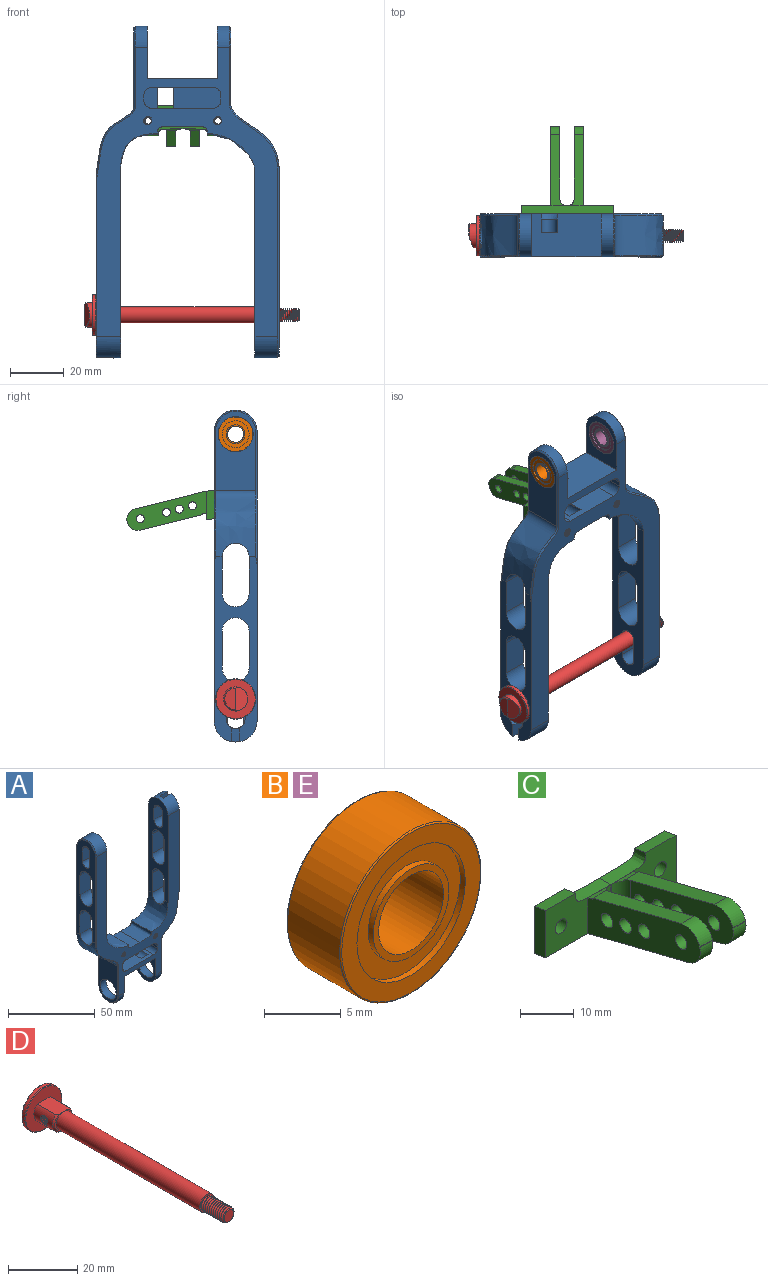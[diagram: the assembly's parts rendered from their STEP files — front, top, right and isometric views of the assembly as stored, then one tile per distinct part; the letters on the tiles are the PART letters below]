
ASSEMBLY  parts=5 mates=6
PART A: 93 faces, bbox 69.1x16.9x123.8 mm
  f0: plane 107.79x67.84mm, normal (0,1,0), area 2068.3mm2, adj f2,f7,f8,f10,f11,f12,f14,f17
  f1: cylinder r=3mm len=11.6mm, axis (0,1,0), area 58mm2, adj f2,f4,f5,f6,f60,f62,f63,f68
  f2: cone r=5mm half-angle=45deg, axis (0,1,0), area 8.4mm2, adj f0,f1,f67,f69
  f3: plane 22.7x8mm, normal (0,0,-1), area 148mm2, adj f5,f6,f9,f50,f55,f62,f63,f64
  f4: plane 22.7x8mm, normal (0,0,1), area 150.1mm2, adj f1,f5,f6,f9,f52,f53,f60
  f5: plane 17.84x7.8mm, normal (0,-1,0), area 133.9mm2, adj f1,f3,f4,f50,f51,f52,f62
  f6: plane 7.8x5.24mm, normal (0,-1,0), area 35.6mm2, adj f1,f3,f4,f53,f54,f55,f63
  f7: cylinder r=1.2mm len=16mm, axis (0,-1,0), area 20.2mm2, adj f0,f9,f58,f59
  f8: cylinder r=1.2mm len=16mm, axis (0,-1,0), area 20.2mm2, adj f0,f9,f56,f57
  f9: plane 107.79x67.84mm, normal (0,-1,0), area 2002.5mm2, adj f3,f4,f7,f8,f10,f11,f12,f14
  f10: plane 68.86x16mm, normal (1,0,0), area 572.6mm2, adj f0,f9,f11,f21,f35,f36,f37,f38
  f11: cylinder r=8mm len=16mm, axis (1,0,0), area 206.6mm2, adj f0,f9,f10,f14,f47,f48,f49
  f12: plane 69x16mm, normal (1,0,0), area 600.9mm2, adj f0,f9,f25,f26,f31,f32,f33,f34
  f13: plane 68.5x15mm, normal (-1,0,0), area 527.7mm2, adj f15,f31,f32,f33,f34,f43,f44,f45
  f14: plane 69x16mm, normal (-1,0,0), area 589.2mm2, adj f0,f9,f11,f22,f35,f36,f37,f38
  f15: extruded ~25.4x18mm, area 454.7mm2, adj f13,f16,f31,f75,f76
  f16: plane 28.5x15mm, normal (-1,0,0), area 270.6mm2, adj f15,f30,f72,f73,f74
  f17: plane 19.6x16mm, normal (1,0,0), area 153.4mm2, adj f0,f9,f18,f28,f30
  f18: plane 26x16mm, normal (0,0,-1), area 375.4mm2, adj f0,f9,f17,f19,f69,f70,f71
  f19: plane 19.6x16mm, normal (-1,0,0), area 153.4mm2, adj f0,f9,f18,f27,f29
  f20: plane 29.5x15mm, normal (1,0,0), area 285.6mm2, adj f21,f29,f81,f82,f83
  f21: extruded ~24.45x15mm, area 410.1mm2, adj f10,f20,f38,f80,f84
  f22: extruded ~16x14.45mm, area 334.6mm2, adj f0,f9,f14,f23,f38
  f23: extruded ~16x9.2mm, area 176.4mm2, adj f0,f9,f22,f24
  f24: extruded ~16x9.2mm, area 176.4mm2, adj f0,f9,f23,f25
  f25: extruded ~17.8x16mm, area 360.2mm2, adj f0,f9,f12,f24,f31
  f26: cylinder r=8mm len=16mm, axis (1,0,0), area 213.6mm2, adj f0,f9,f12,f79
  f27: cylinder r=8mm len=16mm, axis (-1,0,0), area 113.1mm2, adj f0,f9,f19,f82
  f28: cylinder r=8mm len=16mm, axis (-1,0,0), area 113.1mm2, adj f0,f9,f17,f72
  f29: cylinder r=6.5mm len=13mm, axis (1,0,0), area 204.2mm2, adj f19,f20
  f30: cylinder r=6.5mm len=13mm, axis (1,0,0), area 204.2mm2, adj f16,f17
  f31: cylinder r=5mm len=10.33mm, axis (1,0,0), area 148.4mm2, adj f12,f13,f15,f25,f32,f34
  f32: plane 13.7x9mm, normal (0,1,0), area 123.3mm2, adj f12,f13,f31,f33
  f33: cylinder r=5mm len=10mm, axis (1,0,0), area 141.4mm2, adj f12,f13,f32,f34
  f34: plane 13.7x9mm, normal (0,-1,0), area 123.3mm2, adj f12,f13,f31,f33
  f35: plane 13.7x9mm, normal (0,-1,0), area 123.3mm2, adj f10,f14,f36,f38
  f36: cylinder r=5mm len=10mm, axis (1,0,0), area 141.4mm2, adj f10,f14,f35,f37
  f37: plane 13.7x9mm, normal (0,1,0), area 123.3mm2, adj f10,f14,f36,f38
  f38: cylinder r=5mm len=10mm, axis (1,0,0), area 137mm2, adj f10,f14,f21,f22,f35,f37
  f39: cylinder r=5mm len=10mm, axis (1,0,0), area 141.4mm2, adj f10,f14,f40,f42
  f40: plane 13.7x9mm, normal (0,-1,0), area 123.3mm2, adj f10,f14,f39,f41
  f41: cylinder r=5mm len=10mm, axis (1,0,0), area 141.4mm2, adj f10,f14,f40,f42
  f42: plane 13.7x9mm, normal (0,1,0), area 123.3mm2, adj f10,f14,f39,f41
  f43: plane 13.7x9mm, normal (0,1,0), area 123.3mm2, adj f12,f13,f44,f46
  f44: cylinder r=5mm len=10mm, axis (1,0,0), area 141.4mm2, adj f12,f13,f43,f45
  f45: plane 13.7x9mm, normal (0,-1,0), area 123.3mm2, adj f12,f13,f44,f46
  f46: cylinder r=5mm len=10mm, axis (1,0,0), area 141.4mm2, adj f12,f13,f43,f45
  f47: plane 6.5x5.2mm, normal (0,-1,0), area 33.8mm2, adj f10,f11,f49,f88
  f48: plane 6.5x5.2mm, normal (0,1,0), area 33.8mm2, adj f10,f11,f49,f88
  f49: plane 5.34x3mm, normal (1,0,0), area 15.2mm2, adj f11,f47,f48,f88
  f50: cylinder r=3mm len=8mm, axis (0,-1,0), area 37.7mm2, adj f3,f5,f9,f51
  f51: plane 8x1.8mm, normal (1,0,0), area 14.4mm2, adj f5,f9,f50,f52
  f52: cylinder r=3mm len=8mm, axis (0,-1,0), area 37.7mm2, adj f4,f5,f9,f51
  f53: cylinder r=3mm len=8mm, axis (0,-1,0), area 37.7mm2, adj f4,f6,f9,f54
  f54: plane 8x1.8mm, normal (-1,0,0), area 14.4mm2, adj f6,f9,f53,f55
  f55: cylinder r=3mm len=8mm, axis (0,-1,0), area 37.7mm2, adj f3,f6,f9,f54
  f56: bspline ~16.5x3.75mm, area 138.9mm2, adj f0,f8,f9,f57
  f57: bspline ~16.58x3.75mm, area 139mm2, adj f0,f8,f9,f56
  f58: bspline ~16.5x3.75mm, area 138.9mm2, adj f0,f7,f9,f59
  f59: bspline ~16.58x3.75mm, area 139mm2, adj f0,f7,f9,f58
  f60: plane 5.62x1.95mm, normal (0,1,0), area 8mm2, adj f1,f4
  f61: cylinder r=3mm len=11.6mm, axis (0,1,0), area 109.3mm2, adj f62,f63,f64,f65
  f62: plane 11.6x7mm, normal (1,0,0), area 43.4mm2, adj f1,f3,f5,f61,f64,f66
  f63: plane 11.6x7mm, normal (-1,0,0), area 43.4mm2, adj f1,f3,f6,f61,f64,f67
  f64: plane 6x3.25mm, normal (0,1,0), area 15.6mm2, adj f3,f61,f62,f63
  f65: cone r=5mm half-angle=45deg, axis (0,1,0), area 35.5mm2, adj f0,f61,f66,f67
  f66: plane 7x2mm, normal (0.71,0.71,0), area 19.8mm2, adj f0,f62,f65,f68
  f67: plane 7x2mm, normal (-0.71,0.71,0), area 19.8mm2, adj f0,f2,f63,f65
  f68: cone r=5mm half-angle=45deg, axis (0,1,0), area 8.4mm2, adj f0,f1,f66,f71
  f69: plane 7x3.53mm, normal (-1,0,0), area 20.9mm2, adj f0,f1,f2,f18,f70
  f70: plane 5.8x3.53mm, normal (0,1,0), area 10.9mm2, adj f1,f18,f69,f71
  f71: plane 7x3.53mm, normal (1,0,0), area 20.9mm2, adj f0,f1,f18,f68,f70
  f72: cone r=7.5mm half-angle=45deg, axis (1,0,0), area 17.2mm2, adj f16,f28,f73,f74
  f73: plane 21x0.5mm, normal (-0.71,-0.71,0), area 14.8mm2, adj f9,f16,f72,f75
  f74: plane 21x0.5mm, normal (-0.71,0.71,0), area 14.8mm2, adj f0,f16,f72,f76
  f75: bspline ~25.4x18.51mm, area 23.2mm2, adj f9,f15,f73,f77
  f76: bspline ~25.4x18.51mm, area 23.2mm2, adj f0,f15,f74,f78
  f77: plane 61x0.5mm, normal (-0.71,-0.71,0), area 43.1mm2, adj f9,f13,f75,f79
  f78: plane 61x0.5mm, normal (-0.71,0.71,0), area 43.1mm2, adj f0,f13,f76,f79
  f79: cone r=7.5mm half-angle=45deg, axis (1,0,0), area 17.2mm2, adj f13,f26,f77,f78
  f80: bspline ~28.98x15.28mm, area 22.2mm2, adj f9,f10,f21,f81
  f81: plane 22x0.5mm, normal (0.71,-0.71,0), area 15.6mm2, adj f9,f20,f80,f82
  f82: cone r=7.5mm half-angle=45deg, axis (-1,0,0), area 17.2mm2, adj f20,f27,f81,f83
  f83: plane 22x0.5mm, normal (0.71,0.71,0), area 15.6mm2, adj f0,f20,f82,f84
  f84: bspline ~28.98x15.28mm, area 22.2mm2, adj f0,f10,f21,f83
  f85: plane 9x8mm, normal (0,-1,0), area 72mm2, adj f10,f14,f87,f88
  f86: plane 9x8mm, normal (0,1,0), area 72mm2, adj f10,f14,f87,f88
  f87: cylinder r=3.5mm len=9mm, axis (1,0,0), area 99mm2, adj f10,f14,f85,f86
  f88: cylinder r=3.5mm len=9mm, axis (1,0,0), area 78.8mm2, adj f10,f14,f47,f48,f49,f85,f86
  f89: cylinder r=3mm len=9mm, axis (-1,0,0), area 84.8mm2, adj f12,f13,f90,f92
  f90: plane 9x9mm, normal (0,-1,0), area 81mm2, adj f12,f13,f89,f91
  f91: cylinder r=3mm len=9mm, axis (-1,0,0), area 84.8mm2, adj f12,f13,f90,f92
  f92: plane 9x9mm, normal (0,1,0), area 81mm2, adj f12,f13,f89,f91
PART B: 14 faces, bbox 14.1x5x14.1 mm
  f0: plane 7x7mm, normal (0,1,0), area 10.2mm2, adj f2,f9
  f1: plane 7x7mm, normal (0,-1,0), area 10.2mm2, adj f2,f6
  f2: cylinder r=3mm len=6mm, axis (0,1,0), area 94.2mm2, adj f0,f1
  f3: cylinder r=6.5mm len=13mm, axis (0,1,0), area 196mm2, adj f12,f13
  f4: plane 12.8x12.8mm, normal (0,-1,0), area 50.1mm2, adj f8,f12
  f5: plane 12.8x12.8mm, normal (0,1,0), area 50.1mm2, adj f10,f13
  f6: cylinder r=3.5mm len=7mm, axis (0,1,0), area 10.1mm2, adj f1,f7
  f7: plane 10x10mm, normal (0,-1,0), area 40.1mm2, adj f6,f8
  f8: cylinder r=5mm len=10mm, axis (0,1,0), area 14.4mm2, adj f4,f7
  f9: cylinder r=3.5mm len=7mm, axis (0,-1,0), area 11mm2, adj f0,f11
  f10: cylinder r=5mm len=10mm, axis (0,-1,0), area 15.7mm2, adj f5,f11
  f11: plane 10x10mm, normal (0,1,0), area 40.1mm2, adj f9,f10
  f12: torus R=6.4mm, axis (0,-1,0), area 6.4mm2, adj f3,f4
  f13: torus R=6.4mm, axis (0,-1,0), area 6.4mm2, adj f3,f5
PART C: 43 faces, bbox 34.2x32.4x15.1 mm
  f0: plane 8.07x0.3mm, normal (0,-1,0), area 2.4mm2, adj f11,f12,f19,f39,f40
  f1: plane 17.08x10.7mm, normal (0,-1,0), area 104mm2, adj f2,f12,f13,f14,f19,f21,f28
  f2: plane 5.85x1.21mm, normal (0,0.24,0.97), area 5.4mm2, adj f1,f3,f28,f39
  f3: plane 3.72x0.07mm, normal (0,0.97,-0.24), area 0.3mm2, adj f2,f28,f39,f41
  f4: plane 23.1x5.77mm, normal (0,0.24,0.97), area 79.8mm2, adj f28,f33,f35,f39,f41
  f5: plane 3.35x0.1mm, normal (0,-0.97,0.24), area 0.3mm2, adj f28,f33,f35,f36
  f6: plane 26.39x6.58mm, normal (0,-0.24,-0.97), area 92.5mm2, adj f19,f28,f33,f36,f39
  f7: cylinder r=1.5mm len=3.35mm, axis (1,0,0), area 31.6mm2, adj f28,f33
  f8: cylinder r=1.5mm len=3.35mm, axis (1,0,0), area 31.6mm2, adj f28,f33
  f9: cylinder r=1.5mm len=3.35mm, axis (1,0,0), area 31.6mm2, adj f28,f33
  f10: cylinder r=1.5mm len=3.35mm, axis (1,0,0), area 31.6mm2, adj f28,f33
  f11: extruded ~9.2x3mm, area 32mm2, adj f0,f12,f17,f18,f20
  f12: extruded ~9.2x3mm, area 32mm2, adj f0,f1,f11,f18,f21
  f13: plane 11.2x3mm, normal (-1,0,0), area 32.1mm2, adj f1,f18,f19,f21
  f14: cylinder r=1.55mm len=3.1mm, axis (0,1,0), area 29.2mm2, adj f1,f18
  f15: plane 11.2x3mm, normal (1,0,0), area 32.1mm2, adj f17,f18,f19,f20
  f16: cylinder r=1.55mm len=3.1mm, axis (0,1,0), area 29.2mm2, adj f17,f18
  f17: plane 17.12x10.7mm, normal (0,-1,0), area 104mm2, adj f11,f15,f16,f19,f20,f22,f27
  f18: plane 34.2x11.2mm, normal (0,1,0), area 314mm2, adj f11,f12,f13,f14,f15,f16,f19,f20
  f19: plane 34.2x3mm, normal (0,-0.16,-0.99), area 104mm2, adj f0,f1,f6,f13,f15,f17,f18,f26
  f20: plane 7.94x3.02mm, normal (0,0.16,0.99), area 24.1mm2, adj f11,f15,f17,f18
  f21: plane 7.9x3.02mm, normal (0,0.16,0.99), area 24mm2, adj f1,f12,f13,f18
  f22: plane 5.85x1.21mm, normal (0,0.24,0.97), area 5.4mm2, adj f17,f23,f27,f40
  f23: plane 3.72x0.07mm, normal (0,0.97,-0.24), area 0.3mm2, adj f22,f27,f40,f42
  f24: plane 23.1x5.77mm, normal (0,0.24,0.97), area 79.8mm2, adj f27,f34,f37,f40,f42
  f25: plane 3.35x0.1mm, normal (0,-0.97,0.24), area 0.3mm2, adj f27,f34,f37,f38
  f26: plane 26.39x6.58mm, normal (0,-0.24,-0.97), area 92.5mm2, adj f19,f27,f34,f38,f40
  f27: plane 29.42x14.56mm, normal (1,0,0), area 209mm2, adj f17,f22,f23,f24,f25,f26,f29,f30
  f28: plane 29.42x14.56mm, normal (-1,0,0), area 209mm2, adj f1,f2,f3,f4,f5,f6,f7,f8
  f29: cylinder r=1.5mm len=3.35mm, axis (1,0,0), area 31.6mm2, adj f27,f34
  f30: cylinder r=1.5mm len=3.35mm, axis (1,0,0), area 31.6mm2, adj f27,f34
  f31: cylinder r=1.5mm len=3.35mm, axis (1,0,0), area 31.6mm2, adj f27,f34
  f32: cylinder r=1.5mm len=3.35mm, axis (1,0,0), area 31.6mm2, adj f27,f34
  f33: plane 26.92x13.94mm, normal (1,0,0), area 188.5mm2, adj f4,f5,f6,f7,f8,f9,f10,f35
  f34: plane 26.92x13.94mm, normal (-1,0,0), area 188.5mm2, adj f24,f25,f26,f29,f30,f31,f32,f37
  f35: cylinder r=4mm len=4.85mm, axis (-1,0,0), area 21mm2, adj f4,f5,f28,f33
  f36: cylinder r=4mm len=4.85mm, axis (-1,0,0), area 21mm2, adj f5,f6,f28,f33
  f37: cylinder r=4mm len=4.85mm, axis (-1,0,0), area 21mm2, adj f24,f25,f27,f34
  f38: cylinder r=4mm len=4.85mm, axis (-1,0,0), area 21mm2, adj f25,f26,f27,f34
  f39: cylinder r=2.5mm len=8.97mm, axis (0,0,1), area 32.1mm2, adj f0,f2,f3,f4,f6,f33,f41
  f40: cylinder r=2.5mm len=8.97mm, axis (0,0,-1), area 32.1mm2, adj f0,f22,f23,f24,f26,f34,f42
  f41: plane 3.72x0.24mm, normal (0,0.86,0.52), area 1mm2, adj f3,f4,f28,f39
  f42: plane 3.72x0.24mm, normal (0,0.86,0.52), area 1mm2, adj f23,f24,f27,f40
PART D: 26 faces, bbox 15.1x80.4x15.1 mm
  f0: plane 8x4mm, normal (0,1,0), area 25.1mm2, adj f1,f25
  f1: cone r=4mm half-angle=45deg, axis (0,-1,0), area 10.3mm2, adj f0,f2,f25
  f2: cylinder r=4.5mm len=9mm, axis (0,-1,0), area 55.3mm2, adj f1,f3,f25
  f3: plane 14.6x14.6mm, normal (0,1,0), area 103.8mm2, adj f2,f4
  f4: cone r=7.5mm half-angle=45deg, axis (0,-1,0), area 13.2mm2, adj f3,f5
  f5: cylinder r=7.5mm len=15mm, axis (0,1,0), area 54.2mm2, adj f4,f6
  f6: cone r=7.3mm half-angle=45deg, axis (0,1,0), area 13.2mm2, adj f5,f7
  f7: plane 14.6x14.6mm, normal (0,-1,0), area 120.8mm2, adj f6,f8,f19
  f8: plane 8.06x5.36mm, normal (0,0,1), area 41.9mm2, adj f7,f9,f10,f19
  f9: cone r=3.5mm half-angle=45deg, axis (0,1,0), area 13.3mm2, adj f8,f10,f19
  f10: plane 7x6.5mm, normal (0,-1,0), area 9.5mm2, adj f8,f9,f11
  f11: cylinder r=2.98mm len=58.5mm, axis (0,1,0), area 1093.5mm2, adj f10,f12
  f12: plane 5.95x5.95mm, normal (0,-1,0), area 8.2mm2, adj f11,f13
  f13: cylinder r=2.5mm len=8.5mm, axis (0,-1,0), area 8.5mm2, adj f12,f14,f15,f17,f18
  f14: plane 0.79x0.68mm, normal (-1,0,0), area 0.3mm2, adj f13,f15,f18
  f15: bspline ~9.2x5.77mm, area 115.5mm2, adj f13,f14,f16,f17,f18
  f16: plane 4.07x3.9mm, normal (0,-1,0), area 12.3mm2, adj f15,f17,f18
  f17: cone r=2mm half-angle=45deg, axis (0,1,0), area 3.6mm2, adj f13,f15,f16,f18
  f18: bspline ~9.2x5.77mm, area 109.9mm2, adj f13,f14,f15,f16,f17
  f19: cylinder r=4mm len=8mm, axis (0,1,0), area 132.5mm2, adj f7,f8,f9,f20,f21,f22,f23,f24
  f20: cylinder r=1.2mm len=0.55mm, axis (1,0,0), area 0mm2, adj f19,f22
  f21: bspline ~0.56x0.07mm, area 0mm2, adj f19,f22
  f22: bspline ~8.15x3.25mm, area 67.8mm2, adj f19,f20,f21,f23,f24
  f23: cylinder r=1.2mm len=7.69mm, axis (1,0,0), area 1.2mm2, adj f19,f22,f24
  f24: bspline ~8.15x3.25mm, area 67.8mm2, adj f19,f22,f23
  f25: plane 8.68x4.54mm, normal (0,0.93,0.37), area 33.6mm2, adj f0,f1,f2
PART E: same geometry as B
PLACE A rot(axis=(0,1,0),180deg) t=(-6.19,-78.04,53.56)mm
PLACE B rot(axis=(0.58,-0.58,0.58),120deg) t=(-24.29,-86.04,168.06)mm
PLACE C rot(axis=(1,0,0),180deg) t=(-5.94,-78.04,141.76)mm
PLACE D rot(axis=(0.58,-0.58,0.58),120deg) t=(-39.74,-86.04,69.61)mm
PLACE E rot(axis=(-0.58,0.58,0.58),120deg) t=(6.81,-86.04,168.06)mm
MATE parallel A.f86 <-> D.f8  axis (0,1,0) through (-33.69,-89.54,66.11)mm
MATE parallel A.f91 <-> D.f1  axis (-1,0,0) through (-38.19,-86.04,70.11)mm
MATE fastened C.f14 <-> A.f7  axis (0,-1,0) through (-18.94,-78.04,141.76)mm
MATE revolute E.f2 <-> A.f29  axis (1,0,0) through (11.81,-86.04,168.06)mm
MATE revolute B.f2 <-> A.f29  axis (1,0,0) through (-24.19,-86.04,168.06)mm
MATE pin_slot D.f1 <-> A.f91  axis (1,0,0) through (-38.19,-86.04,69.61)mm
